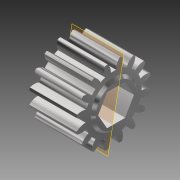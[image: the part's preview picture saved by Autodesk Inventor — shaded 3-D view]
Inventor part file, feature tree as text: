
AUTODESK INVENTOR PART (.ipt)
format: ipt  version: 2016 SP1 (Build 200210100, 210)  size: 207,872 bytes
history: native  units: in
note: dims shown in document units (in); Inventor stores cm internally (conversion verified against a paired STEP export)
features: plane x1, other x1
ambient origin geometry x8: Origin, YZ Plane, XZ Plane, XY Plane, X Axis, Y Axis, Z Axis, Center Point
bodies: Solid1 (feature_tree)
feature tree (2):
  plane  "Work Plane1"
  other  "Bore"
